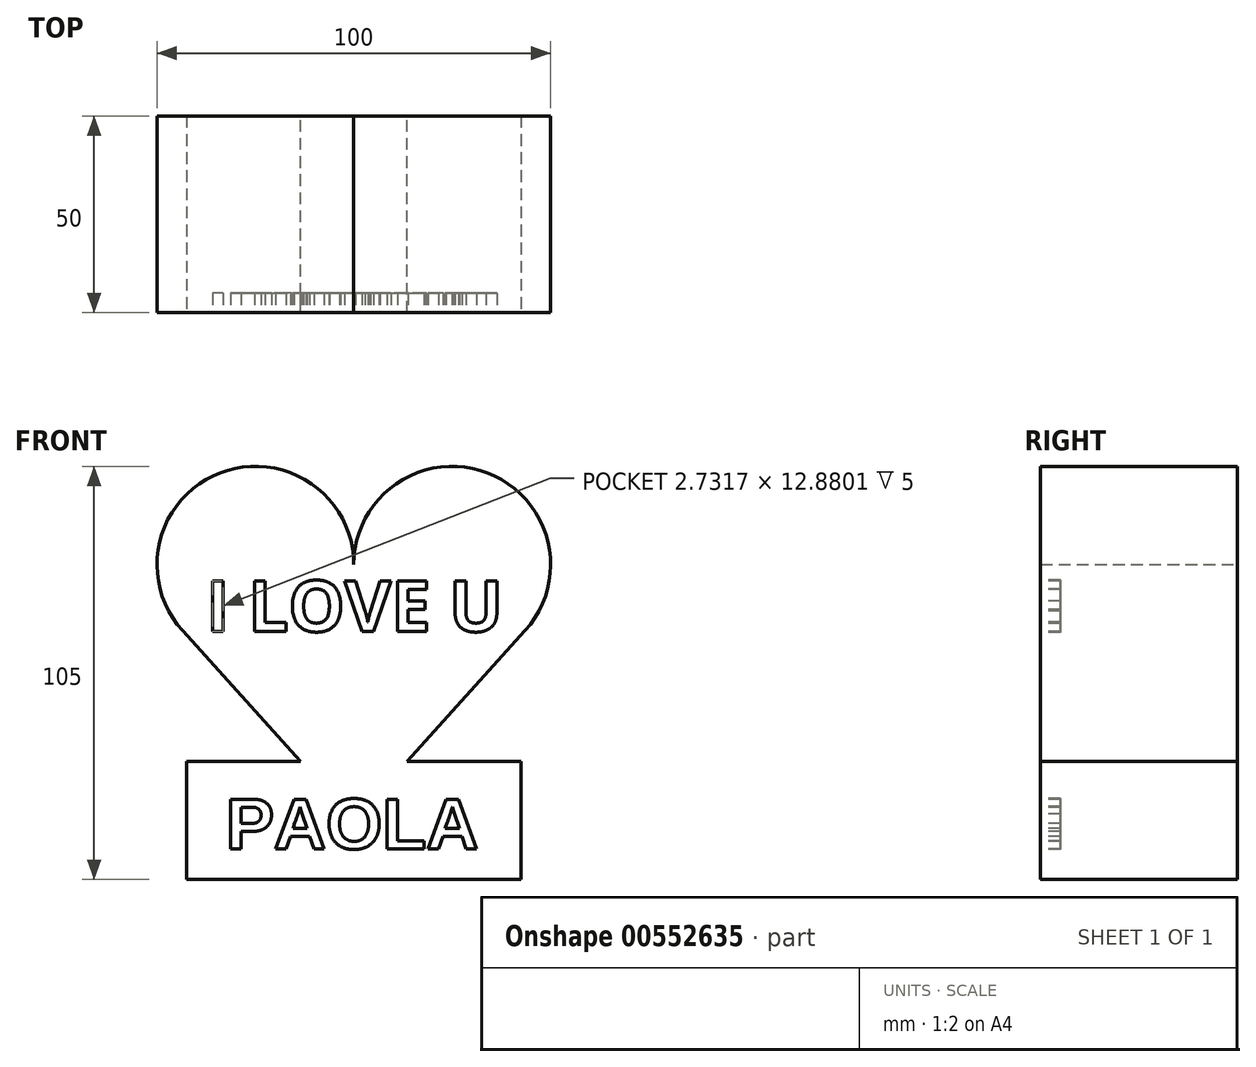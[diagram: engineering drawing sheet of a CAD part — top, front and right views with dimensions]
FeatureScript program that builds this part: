
annotation { "Feature Type Name" : "Feature", "Feature Type Description" : "" }
export const myFeature = defineFeature(function(context is Context, id is Id, definition is map)
    precondition{}
    {
        {
            var Q0;
            Q0=qCreatedBy(makeId("Front.planeOp"),FACE);
            var sketch = newSketch(context, id + "F0", { "sketchPlane" : qUnion([Q0])});
            skArc(sketch, "E0", {"start": v(0, 0) * mm, "mid": v(-33.97, 23.33) * mm, "end": v(-43.56, -16.75) * mm});
            skArc(sketch, "E1", {"start": v(43.56, -16.75) * mm, "mid": v(33.97, 23.33) * mm, "end": v(0, 0) * mm});
            skLineSegment(sketch, "E2", {"start": v(0, 0) * mm, "end": v(0, -65) * mm, "construction": true});
            skLineSegment(sketch, "E3", {"start": v(0, -65) * mm, "end": v(-43.56, -16.75) * mm});
            skLineSegment(sketch, "E4", {"start": v(0, -65) * mm, "end": v(43.56, -16.75) * mm});
            skPoint(sketch, "E5.orphan", {"position": v(-58.68, 0) * mm});
            skPoint(sketch, "E6.orphan", {"position": v(58.68, 0) * mm});
            skLineSegment(sketch, "E7", {"start": v(0, 0) * mm, "end": v(0, -65) * mm});
            skSolve(sketch);
        }
        {
            var Q0;
            Q0=makeQuery(id+"F0.imprint","IMPRINT",FACE,{"disambiguationData":[TD([[makeQuery(id+"F0.imprint","IMPRINT",EDGE,{"derivedFrom":sQuery(id+"F0.wireOp",EDGE,"E1")}),1.0]])]});
            var Q1;
            Q1=makeQuery(id+"F0.imprint","IMPRINT",FACE,{"disambiguationData":[TD([[makeQuery(id+"F0.imprint","IMPRINT",EDGE,{"derivedFrom":sQuery(id+"F0.wireOp",EDGE,"E0")}),1.0]])]});
            extrude(context, id + "F1", {"entities" : qUnion([Q0, Q1]), "depth" : 50 * mm, "offsetDistance" : 25 * mm});
        }
        {
            var Q0;
            Q0=makeQuery(id+"F1.opExtrude","CAP_FACE",FACE,{"disambiguationData":[OSD([sQuery(id+"F0.wireOp",EDGE,"E0"),sQuery(id+"F0.wireOp",EDGE,"E1"),sQuery(id+"F0.wireOp",EDGE,"E3"),sQuery(id+"F0.wireOp",EDGE,"E4")])],"isStart":false});
            var sketch = newSketch(context, id + "F2", { "sketchPlane" : qUnion([Q0])});
            skText(sketch, "E8", { "text": "I LOVE U", "fontName": "OpenSans-Bold.ttf"});
            const initialGuessF2  = {"E8": [-0.0375, -0.01699, 1, 0, 0.01299]};
            skSetInitialGuess(sketch, initialGuessF2);
            skSolve(sketch);
        }
        {
            var Q0;
            Q0=qSketchRegion(id+"F2",true);
            extrude(context, id + "F3", {"entities" : qUnion([Q0]), "operationType" : NewBodyOperationType.REMOVE, "oppositeDirection" : true, "depth" : 5 * mm, "offsetDistance" : 25 * mm});
        }
        {
            var Q0;
            {var subQ0=sQuery(id+"F0.wireOp",EDGE,"E3");var subQ1=sQuery(id+"F0.wireOp",EDGE,"E0");var subQ2=sQuery(id+"F0.wireOp",EDGE,"E4");var subQ3=sQuery(id+"F0.wireOp",EDGE,"E1");Q0=makeQuery(id+"F3.boolean.opBoolean","SPLIT",FACE,{"disambiguationData":[TD([makeQuery(id+"F1.opExtrude","SWEPT_FACE",FACE,{"disambiguationData":[OSD([subQ1])]})])],"derivedFrom":makeQuery(id+"F1.opExtrude","CAP_FACE",FACE,{"disambiguationData":[OSD([subQ1,subQ3,subQ0,subQ2])],"isStart":false})});}
            var sketch = newSketch(context, id + "F4", { "sketchPlane" : qUnion([Q0])});
            skLineSegment(sketch, "E9.bottom", {"start": v(42.5, -50) * mm, "end": v(-42.5, -50) * mm});
            skLineSegment(sketch, "E9.top", {"start": v(42.5, -80) * mm, "end": v(-42.5, -80) * mm});
            skLineSegment(sketch, "E9.left", {"start": v(42.5, -50) * mm, "end": v(42.5, -80) * mm});
            skLineSegment(sketch, "E9.right", {"start": v(-42.5, -50) * mm, "end": v(-42.5, -80) * mm});
            skPoint(sketch, "E9.middle", {"position": v(0, -65) * mm});
            skSolve(sketch);
        }
        {
            var Q0;
            Q0 = qSketchRegion(id + "F4", true);
            extrude(context, id + "F5", {"entities" : qUnion([Q0]), "operationType" : NewBodyOperationType.ADD, "oppositeDirection" : true, "depth" : 50 * mm, "offsetDistance" : 25 * mm});
        }
        {
            var Q0;
            {var subQ0=sQuery(id+"F0.wireOp",EDGE,"E3");var subQ1=sQuery(id+"F0.wireOp",EDGE,"E0");var subQ2=sQuery(id+"F0.wireOp",EDGE,"E4");var subQ3=sQuery(id+"F0.wireOp",EDGE,"E1");Q0=makeQuery(id+"F5.boolean.opBoolean","MERGE",FACE,{"derivedFrom":[makeQuery(id+"F3.boolean.opBoolean","SPLIT",FACE,{"disambiguationData":[TD([makeQuery(id+"F1.opExtrude","SWEPT_FACE",FACE,{"disambiguationData":[OSD([subQ1])]})])],"derivedFrom":makeQuery(id+"F1.opExtrude","CAP_FACE",FACE,{"disambiguationData":[OSD([subQ1,subQ3,subQ0,subQ2])],"isStart":false})}),makeQuery(id+"F5.opExtrude","CAP_FACE",FACE,{"disambiguationData":[OSD([sQuery(id+"F4.wireOp",EDGE,"E9.bottom"),sQuery(id+"F4.wireOp",EDGE,"E9.top"),sQuery(id+"F4.wireOp",EDGE,"E9.left"),sQuery(id+"F4.wireOp",EDGE,"E9.right")])],"isStart":true})]});}
            var sketch = newSketch(context, id + "F6", { "sketchPlane" : qUnion([Q0])});
            skText(sketch, "E10", { "text": "PAOLA", "fontName": "Arimo-Bold.ttf"});
            const initialGuessF6  = {"E10": [-0.0325, -0.0722, 1, 0, 0.0132]};
            skSetInitialGuess(sketch, initialGuessF6);
            skSolve(sketch);
        }
        {
            var Q0;
            Q0 = qSketchRegion(id + "F6", true);
            extrude(context, id + "F7", {"entities" : qUnion([Q0]), "operationType" : NewBodyOperationType.REMOVE, "oppositeDirection" : true, "depth" : 5 * mm, "offsetDistance" : 25 * mm});
        }
    });
